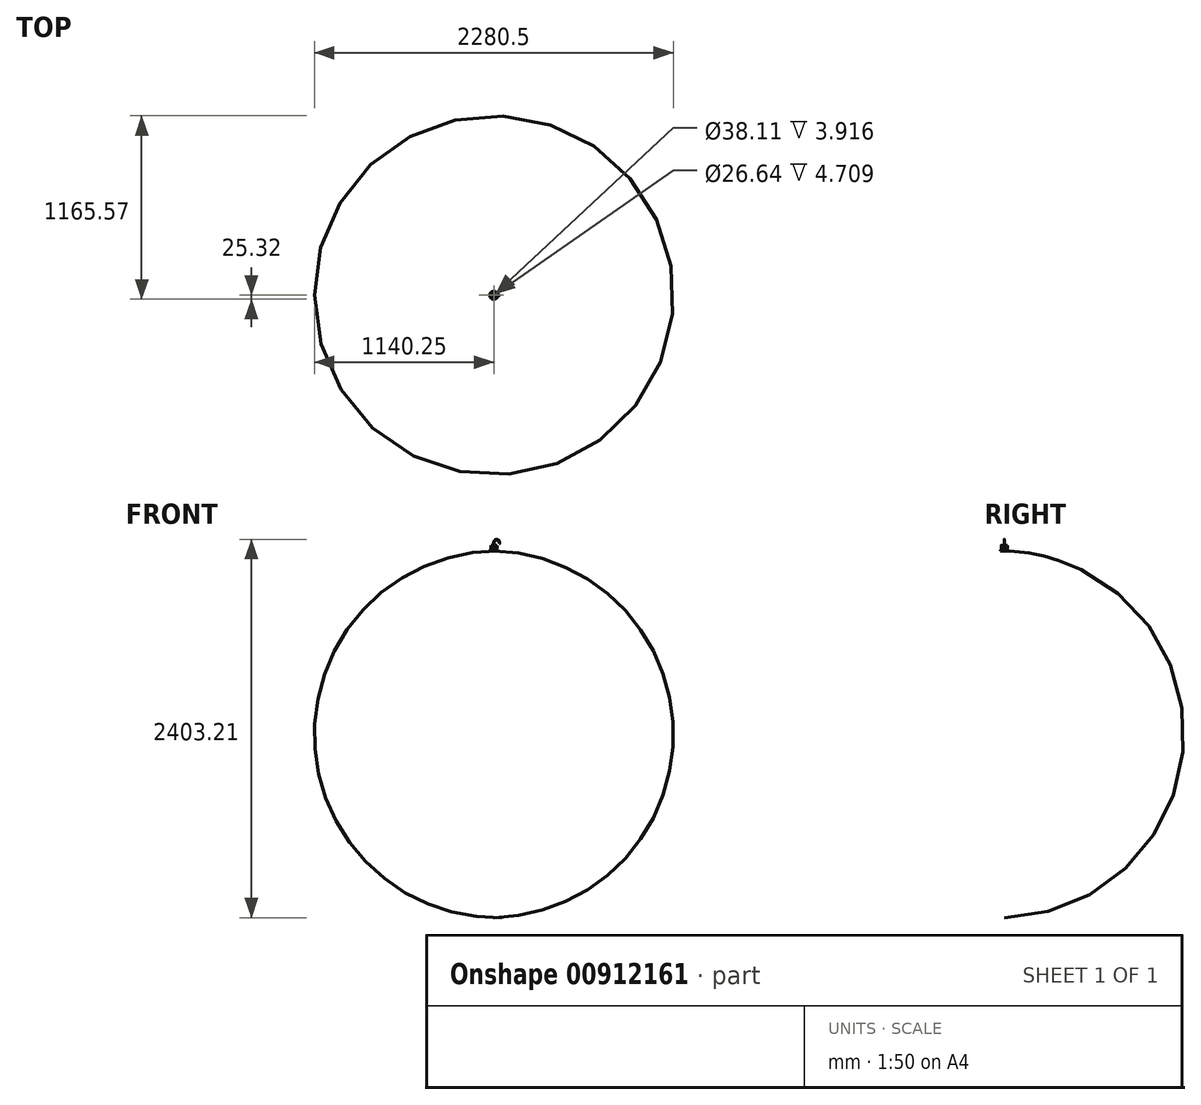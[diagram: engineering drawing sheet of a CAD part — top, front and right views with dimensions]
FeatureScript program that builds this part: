
annotation { "Feature Type Name" : "Feature", "Feature Type Description" : "" }
export const myFeature = defineFeature(function(context is Context, id is Id, definition is map)
    precondition{}
    {
        {
            var Q0;
            Q0=qCreatedBy(makeId("Front.planeOp"),FACE);
            var sketch = newSketch(context, id + "F0", { "sketchPlane" : qUnion([Q0])});
            skArc(sketch, "E0", {"start": v(0, 40.72) * mm, "mid": v(-12.66, 40.92) * mm, "end": v(-25.32, 40.98) * mm});
            skArc(sketch, "E1", {"start": v(-25.32, 40.98) * mm, "mid": v(-30.3, -0.78) * mm, "end": v(-25.32, -42.55) * mm});
            skArc(sketch, "E2", {"start": v(-25.32, -42.55) * mm, "mid": v(-13.77, -50.15) * mm, "end": v(0, -51.43) * mm});
            skLineSegment(sketch, "E3", {"start": v(0, 38.63) * mm, "end": v(0, 40.72) * mm});
            skLineSegment(sketch, "E4", {"start": v(0, 40.72) * mm, "end": v(0, -51.43) * mm});
            skLineSegment(sketch, "E5", {"start": v(-24.02, 40.98) * mm, "end": v(-25.32, 40.98) * mm});
            skArc(sketch, "E6", {"start": v(-13.32, 52.98) * mm, "mid": v(-21.08, 48.75) * mm, "end": v(-25.32, 40.98) * mm});
            skLineSegment(sketch, "E7", {"start": v(-13.32, 52.98) * mm, "end": v(0, 52.98) * mm});
            skLineSegment(sketch, "E8", {"start": v(0, 40.72) * mm, "end": v(0, 52.98) * mm});
            skLineSegment(sketch, "E9", {"start": v(-13.32, 52.98) * mm, "end": v(-13.32, 57.7) * mm});
            skLineSegment(sketch, "E10", {"start": v(-13.32, 57.7) * mm, "end": v(0, 57.7) * mm});
            skLineSegment(sketch, "E11", {"start": v(0, 57.7) * mm, "end": v(0, 52.98) * mm});
            skLineSegment(sketch, "E12", {"start": v(-13.32, 57.7) * mm, "end": v(-19.06, 57.7) * mm});
            skLineSegment(sketch, "E13", {"start": v(-19.06, 57.7) * mm, "end": v(-19.06, 61.6) * mm});
            skLineSegment(sketch, "E14", {"start": v(-19.06, 61.6) * mm, "end": v(0, 61.6) * mm});
            skLineSegment(sketch, "E15", {"start": v(0, 61.6) * mm, "end": v(-13.32, 61.6) * mm});
            skLineSegment(sketch, "E16", {"start": v(-13.32, 61.6) * mm, "end": v(-13.32, 65.26) * mm});
            skLineSegment(sketch, "E17", {"start": v(-13.32, 65.26) * mm, "end": v(0, 65.26) * mm});
            skLineSegment(sketch, "E18", {"start": v(0, 65.26) * mm, "end": v(-19.06, 65.26) * mm});
            skLineSegment(sketch, "E19", {"start": v(-19.06, 65.26) * mm, "end": v(-19.06, 75.96) * mm});
            skLineSegment(sketch, "E20", {"start": v(-19.06, 75.96) * mm, "end": v(0, 75.96) * mm});
            skLineSegment(sketch, "E21", {"start": v(0, 75.96) * mm, "end": v(0, 40.72) * mm});
            skLineSegment(sketch, "E22", {"start": v(-15.92, 65.26) * mm, "end": v(-15.92, 75.96) * mm});
            skLineSegment(sketch, "E23", {"start": v(-15.92, 75.96) * mm, "end": v(-12.53, 75.96) * mm});
            skLineSegment(sketch, "E24", {"start": v(-12.53, 75.96) * mm, "end": v(-12.53, 65.26) * mm});
            skLineSegment(sketch, "E25", {"start": v(-9.53, 75.96) * mm, "end": v(-9.53, 65.26) * mm});
            skLineSegment(sketch, "E26", {"start": v(-6.27, 75.96) * mm, "end": v(-6.27, 65.26) * mm});
            skLineSegment(sketch, "E27", {"start": v(-3.65, 75.96) * mm, "end": v(-3.65, 65.26) * mm});
            skLineSegment(sketch, "E28", {"start": v(-23.7, 45.28) * mm, "end": v(0, 45.28) * mm});
            skSolve(sketch);
        }
        {
            var Q0;
            {var subQ1=sQuery(id+"F0.wireOp",EDGE,"E0");Q0=makeQuery(id+"F0.imprint","IMPRINT",FACE,{"disambiguationData":[TD([[makeQuery(id+"F0.imprint","IMPRINT",EDGE,{"derivedFrom":subQ1}),1.0]])]});}
            var Q1;
            {var subQ1=sQuery(id+"F0.wireOp",EDGE,"E0");Q1=makeQuery(id+"F0.imprint","IMPRINT",FACE,{"disambiguationData":[TD([[makeQuery(id+"F0.imprint","IMPRINT",EDGE,{"derivedFrom":subQ1}),-1.0]])]});}
            var Q2;
            {var subQ0=sQuery(id+"F0.wireOp",EDGE,"E7");Q2=makeQuery(id+"F0.imprint","IMPRINT",FACE,{"disambiguationData":[TD([[makeQuery(id+"F0.imprint","IMPRINT",EDGE,{"derivedFrom":subQ0}),-1.0]])]});}
            var Q3;
            {var subQ0=sQuery(id+"F0.wireOp",EDGE,"E10");Q3=makeQuery(id+"F0.imprint","IMPRINT",FACE,{"disambiguationData":[TD([[makeQuery(id+"F0.imprint","IMPRINT",EDGE,{"derivedFrom":subQ0}),1.0]])]});}
            var Q4;
            {var subQ6=sQuery(id+"F0.wireOp",EDGE,"E15");Q4=makeQuery(id+"F0.imprint","IMPRINT",FACE,{"disambiguationData":[TD([[makeQuery(id+"F0.imprint","IMPRINT",EDGE,{"derivedFrom":subQ6}),-1.0]])]});}
            var Q5;
            {var subQ0=sQuery(id+"F0.wireOp",EDGE,"E19");Q5=makeQuery(id+"F0.imprint","IMPRINT",FACE,{"disambiguationData":[TD([[makeQuery(id+"F0.imprint","IMPRINT",EDGE,{"derivedFrom":subQ0}),-1.0]])]});}
            var Q6;
            {var subQ2=sQuery(id+"F0.wireOp",EDGE,"E22");Q6=makeQuery(id+"F0.imprint","IMPRINT",FACE,{"disambiguationData":[TD([[makeQuery(id+"F0.imprint","IMPRINT",EDGE,{"derivedFrom":subQ2}),-1.0]])]});}
            var Q7;
            {var subQ0=sQuery(id+"F0.wireOp",EDGE,"E24");Q7=makeQuery(id+"F0.imprint","IMPRINT",FACE,{"disambiguationData":[TD([[makeQuery(id+"F0.imprint","IMPRINT",EDGE,{"derivedFrom":subQ0}),1.0]])]});}
            var Q8;
            {var subQ3=sQuery(id+"F0.wireOp",EDGE,"E27");Q8=makeQuery(id+"F0.imprint","IMPRINT",FACE,{"disambiguationData":[TD([[makeQuery(id+"F0.imprint","IMPRINT",EDGE,{"derivedFrom":subQ3}),1.0]])]});}
            var Q9;
            {var subQ0=sQuery(id+"F0.wireOp",EDGE,"E25");Q9=makeQuery(id+"F0.imprint","IMPRINT",FACE,{"disambiguationData":[TD([[makeQuery(id+"F0.imprint","IMPRINT",EDGE,{"derivedFrom":subQ0}),1.0]])]});}
            var Q10;
            {var subQ0=sQuery(id+"F0.wireOp",EDGE,"E26");Q10=makeQuery(id+"F0.imprint","IMPRINT",FACE,{"disambiguationData":[TD([[makeQuery(id+"F0.imprint","IMPRINT",EDGE,{"derivedFrom":subQ0}),1.0]])]});}
            var Q11;
            {var subQ0=sQuery(id+"F0.wireOp",EDGE,"E7");Q11=makeQuery(id+"F0.imprint","IMPRINT",FACE,{"disambiguationData":[TD([[makeQuery(id+"F0.imprint","IMPRINT",EDGE,{"derivedFrom":subQ0}),1.0]])]});}
            var Q12;
            Q12=sQuery(id+"F0.wireOp",EDGE,"E21");
            revolve(context, id + "F1", {"surfaceOperationType" : NewSurfaceOperationType.NEW, "entities" : qUnion([Q0, Q1, Q2, Q3, Q4, Q5, Q6, Q7, Q8, Q9, Q10, Q11]), "axis" : qUnion([Q12]), "revolveType" : RevolveType.FULL});
        }
        {
            var Q0;
            Q0=qCreatedBy(makeId("Front.planeOp"),FACE);
            var sketch = newSketch(context, id + "F2", { "sketchPlane" : qUnion([Q0])});
            skFitSpline(sketch, "E29", {"points": [v(0, 61.88) * mm, v(5.62, 109.05) * mm, v(29.04, 108.86) * mm, v(36.04, 88.21) * mm], "startDerivative": vector(-5.57, 105.39) * mm, "endDerivative": vector(6.07, -79.52) * mm});
            skSolve(sketch);
        }
        {
            var Q0;
            Q0=sQuery(id+"F2.wireOp",VERTEX,"E29.end");
            var Q1;
            Q1=sQuery(id+"F2.wireOp",EDGE,"E29");
            cPlane(context, id + "F3", {"entities" : qUnion([Q0, Q1]), "cplaneType" : CPlaneType.CURVE_POINT, "offset" : 25.4 * mm, "width" : 152.4 * mm, "height" : 152.4 * mm});
        }
        {
            var Q0;
            Q0=qCreatedBy(id+"F3.planeOp",FACE);
            var sketch = newSketch(context, id + "F4", { "sketchPlane" : qUnion([Q0])});
            skCircle(sketch, "E30", {"center": v(42.68, 0) * mm, "radius": 1.2 * mm});
            skSolve(sketch);
        }
        {
            var Q0;
            Q0=makeQuery(id+"F4.imprint","IMPRINT",FACE,{"disambiguationData":[TD([[makeQuery(id+"F4.imprint","IMPRINT",EDGE,{"derivedFrom":sQuery(id+"F4.wireOp",EDGE,"E30")}),1.0]])]});
            var Q1;
            Q1=sQuery(id+"F2.wireOp",EDGE,"E29");
            sweep(context, id + "F5", {"operationType" : NewBodyOperationType.ADD, "profiles" : qUnion([Q0]), "path" : qUnion([Q1])});
        }
    });
